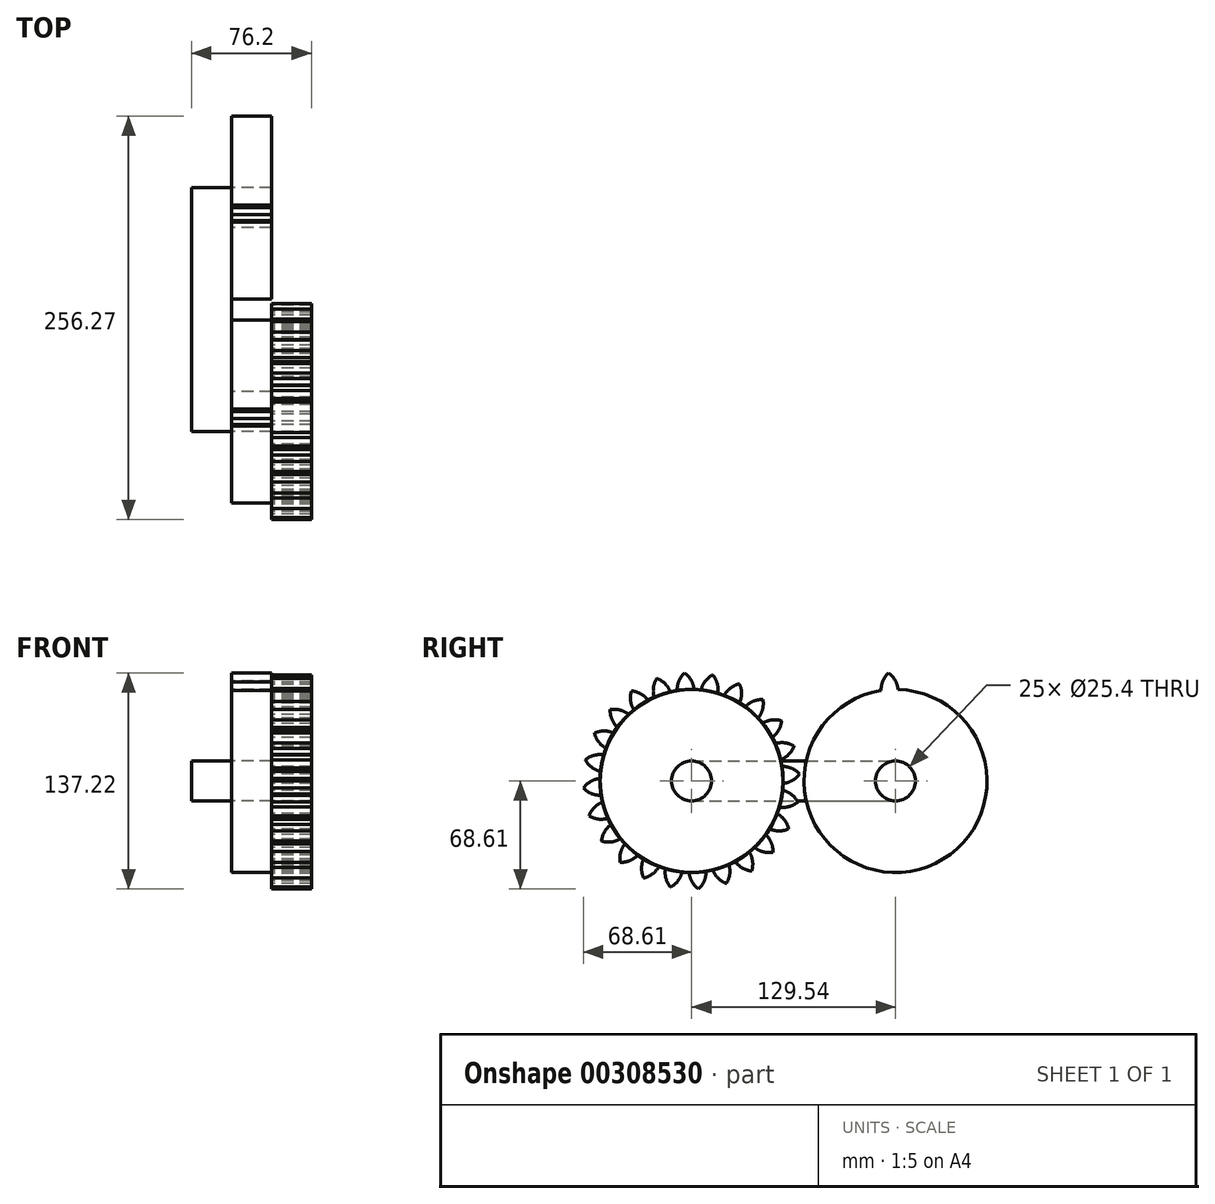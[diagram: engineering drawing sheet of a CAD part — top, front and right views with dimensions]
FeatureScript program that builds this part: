
annotation { "Feature Type Name" : "Feature", "Feature Type Description" : "" }
export const myFeature = defineFeature(function(context is Context, id is Id, definition is map)
    precondition{}
    {
        {
            var Q0;
            Q0=qCreatedBy(makeId("Right.planeOp"),FACE);
            var sketch = newSketch(context, id + "F0", { "sketchPlane" : qUnion([Q0])});
            skLineSegment(sketch, "E0.bottom", {"start": v(0, 0) * mm, "end": v(129.54, 0) * mm});
            skLineSegment(sketch, "E0.top", {"start": v(0, 25.4) * mm, "end": v(129.54, 25.4) * mm});
            skLineSegment(sketch, "E0.left", {"start": v(0, 0) * mm, "end": v(0, 25.4) * mm});
            skLineSegment(sketch, "E0.right", {"start": v(129.54, 0) * mm, "end": v(129.54, 25.4) * mm});
            skCircle(sketch, "E1", {"center": v(0, 12.7) * mm, "radius": 12.7 * mm});
            skCircle(sketch, "E2", {"center": v(129.54, 12.7) * mm, "radius": 12.7 * mm});
            skSolve(sketch);
        }
        {
            var Q0;
            Q0 = qSketchRegion(id + "F0", true);
            extrude(context, id + "F1", {"entities" : qUnion([Q0]), "depth" : 25.4 * mm});
        }
        {
            var Q0;
            {var subQ0=sQuery(id+"F0.wireOp",EDGE,"E0.left");Q0=makeQuery(id+"F0.imprint","IMPRINT",FACE,{"disambiguationData":[TD([[makeQuery(id+"F0.imprint","IMPRINT",EDGE,{"derivedFrom":subQ0}),-1.0]])]});}
            var Q1;
            {var subQ0=sQuery(id+"F0.wireOp",EDGE,"E0.left");Q1=makeQuery(id+"F0.imprint","IMPRINT",FACE,{"disambiguationData":[TD([[makeQuery(id+"F0.imprint","IMPRINT",EDGE,{"derivedFrom":subQ0}),1.0]])]});}
            var Q2;
            {var subQ0=sQuery(id+"F0.wireOp",EDGE,"E0.right");Q2=makeQuery(id+"F0.imprint","IMPRINT",FACE,{"disambiguationData":[TD([[makeQuery(id+"F0.imprint","IMPRINT",EDGE,{"derivedFrom":subQ0}),-1.0]])]});}
            var Q3;
            {var subQ0=sQuery(id+"F0.wireOp",EDGE,"E0.right");Q3=makeQuery(id+"F0.imprint","IMPRINT",FACE,{"disambiguationData":[TD([[makeQuery(id+"F0.imprint","IMPRINT",EDGE,{"derivedFrom":subQ0}),1.0]])]});}
            extrude(context, id + "F2", {"entities" : qUnion([Q0, Q1, Q2, Q3]), "operationType" : NewBodyOperationType.ADD, "depth" : 50.8 * mm});
        }
        {
            var Q0;
            Q0=makeQuery(id+"F2.opExtrude","CAP_FACE",FACE,{"disambiguationData":[OSD([sQuery(id+"F0.wireOp",EDGE,"E1")])],"isStart":false});
            var sketch = newSketch(context, id + "F3", { "sketchPlane" : qUnion([Q0])});
            skCircle(sketch, "E3", {"center": v(0, 12.7) * mm, "radius": 12.7 * mm});
            skCircle(sketch, "E4", {"center": v(0, 12.7) * mm, "radius": 53.72 * mm, "construction": true});
            skCircle(sketch, "E5", {"center": v(0, 12.7) * mm, "radius": 63.5 * mm, "construction": true});
            skCircle(sketch, "E6", {"center": v(0, 12.7) * mm, "radius": 58.67 * mm, "construction": true});
            skLineSegment(sketch, "E7", {"start": v(0, 12.7) * mm, "end": v(0, 119.88) * mm, "construction": true});
            skLineSegment(sketch, "E8", {"start": v(0, 12.7) * mm, "end": v(-7.22, 122.84) * mm, "construction": true});
            skLineSegment(sketch, "E9", {"start": v(0, 76.2) * mm, "end": v(-90.82, 70.25) * mm, "construction": true});
            skLineSegment(sketch, "E10", {"start": v(0, 76.2) * mm, "end": v(-84, 39.24) * mm, "construction": true});
            skCircle(sketch, "E11", {"center": v(0, 12.7) * mm, "radius": 58.12 * mm});
            skCircle(sketch, "E12", {"center": v(0, 76.2) * mm, "radius": 14.6 * mm, "construction": true});
            skCircle(sketch, "E13", {"center": v(-12.9, 69.37) * mm, "radius": 14.6 * mm, "construction": true});
            skArc(sketch, "E14", {"start": v(0, 76.2) * mm, "mid": v(-1.95, 79.02) * mm, "end": v(-4.5, 81.3) * mm});
            skArc(sketch, "E15", {"start": v(1.63, 70.8) * mm, "mid": v(1.05, 73.57) * mm, "end": v(0, 76.2) * mm});
            skArc(sketch, "E16.MirrorCS", {"start": v(-9.2, 70.1) * mm, "mid": v(-8.99, 72.91) * mm, "end": v(-8.29, 75.66) * mm});
            skArc(sketch, "E17.MirrorCS", {"start": v(-8.29, 75.66) * mm, "mid": v(-6.73, 78.7) * mm, "end": v(-4.5, 81.3) * mm});
            skSolve(sketch);
        }
        {
            var Q0;
            Q0 = qSketchRegion(id + "F3", true);
            extrude(context, id + "F4", {"entities" : qUnion([Q0]), "depth" : 25.4 * mm});
        }
        {
            var Q0;
            Q0=makeQuery(id+"F4.opExtrude","SWEPT_BODY",BODY,{"disambiguationData":[OSD([sQuery(id+"F3.wireOp",EDGE,"E3"),sQuery(id+"F3.wireOp",EDGE,"E11"),sQuery(id+"F3.wireOp",EDGE,"E14"),sQuery(id+"F3.wireOp",EDGE,"E15"),sQuery(id+"F3.wireOp",EDGE,"E16.MirrorCS"),sQuery(id+"F3.wireOp",EDGE,"E17.MirrorCS")])]});
            var Q1;
            Q1=makeQuery(id+"F4.opExtrude","SWEPT_FACE",FACE,{"disambiguationData":[OSD([sQuery(id+"F3.wireOp",EDGE,"E11")])]});
            circularPattern(context, id + "F5", {"entities" : qUnion([Q0]), "axis" : qUnion([Q1]), "angle" : 360 * degree, "instanceCount" : 24, "equalSpace" : true});
        }
        {
            var Q0;
            Q0=makeQuery(id+"F4.opExtrude","SWEPT_BODY",BODY,{"disambiguationData":[OSD([sQuery(id+"F3.wireOp",EDGE,"E3"),sQuery(id+"F3.wireOp",EDGE,"E11"),sQuery(id+"F3.wireOp",EDGE,"E14"),sQuery(id+"F3.wireOp",EDGE,"E15"),sQuery(id+"F3.wireOp",EDGE,"E16.MirrorCS"),sQuery(id+"F3.wireOp",EDGE,"E17.MirrorCS")])]});
            transform(context, id + "F6", {"entities" : qUnion([Q0]), "transformType" : TransformType.TRANSLATION_3D, "dx" : 0 * mm, "dy" : 129.54 * mm, "dz" : 0 * mm, "makeCopy" : true});
        }
        {
            var Q0;
            Q0=makeQuery(id+"F4.opExtrude","SWEPT_BODY",BODY,{"disambiguationData":[OSD([sQuery(id+"F3.wireOp",EDGE,"E3"),sQuery(id+"F3.wireOp",EDGE,"E11"),sQuery(id+"F3.wireOp",EDGE,"E14"),sQuery(id+"F3.wireOp",EDGE,"E15"),sQuery(id+"F3.wireOp",EDGE,"E16.MirrorCS"),sQuery(id+"F3.wireOp",EDGE,"E17.MirrorCS")])]});
            var Q1;
            Q1=makeQuery(id+"F6.opPattern","COPY",BODY,{"derivedFrom":makeQuery(id+"F4.opExtrude","SWEPT_BODY",BODY,{"disambiguationData":[OSD([sQuery(id+"F3.wireOp",EDGE,"E3"),sQuery(id+"F3.wireOp",EDGE,"E11"),sQuery(id+"F3.wireOp",EDGE,"E14"),sQuery(id+"F3.wireOp",EDGE,"E15"),sQuery(id+"F3.wireOp",EDGE,"E16.MirrorCS"),sQuery(id+"F3.wireOp",EDGE,"E17.MirrorCS")])]}),"instanceName":"1"});
            transform(context, id + "F7", {"entities" : qUnion([Q0, Q1]), "transformType" : TransformType.TRANSLATION_3D, "dx" : -25.4 * mm, "dy" : 0 * mm, "dz" : 0 * mm, "makeCopy" : false});
        }
    });
